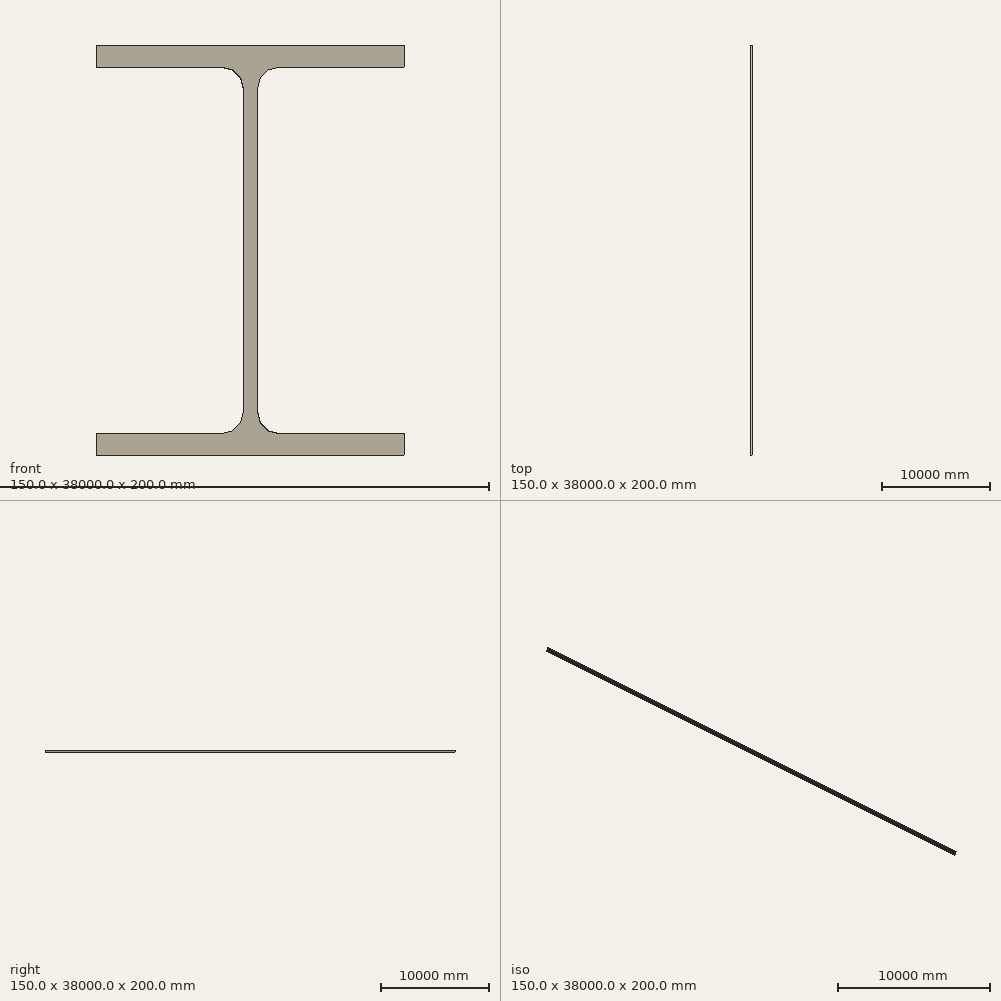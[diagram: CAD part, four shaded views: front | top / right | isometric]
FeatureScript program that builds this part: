
annotation { "Feature Type Name" : "Feature", "Feature Type Description" : "" }
export const myFeature = defineFeature(function(context is Context, id is Id, definition is map)
    precondition{}
    {
        {
            var Q0;
            Q0=qCreatedBy(makeId("Front.planeOp"),FACE);
            var sketch = newSketch(context, id + "F0", { "sketchPlane" : qUnion([Q0])});
            skLineSegment(sketch, "E0.left", {"start": v(3.55, 79.3) * mm, "end": v(3.55, -79.3) * mm});
            skLineSegment(sketch, "E0.right", {"start": v(-3.55, 79.3) * mm, "end": v(-3.55, -79.3) * mm});
            skPoint(sketch, "E0.middle", {"position": v(0, 0) * mm});
            skLineSegment(sketch, "E1.bottom", {"start": v(-75, 89.3) * mm, "end": v(-13.55, 89.3) * mm});
            skLineSegment(sketch, "E1.top", {"start": v(-75, 100) * mm, "end": v(75, 100) * mm});
            skLineSegment(sketch, "E1.left", {"start": v(-75, 89.3) * mm, "end": v(-75, 100) * mm});
            skLineSegment(sketch, "E1.right", {"start": v(75, 89.3) * mm, "end": v(75, 100) * mm});
            skLineSegment(sketch, "E2.bottom", {"start": v(75, -89.3) * mm, "end": v(13.55, -89.3) * mm});
            skLineSegment(sketch, "E2.top", {"start": v(75, -100) * mm, "end": v(-75, -100) * mm});
            skLineSegment(sketch, "E2.left", {"start": v(75, -89.3) * mm, "end": v(75, -100) * mm});
            skLineSegment(sketch, "E2.right", {"start": v(-75, -89.3) * mm, "end": v(-75, -100) * mm});
            skLineSegment(sketch, "E3.trimOffspring", {"start": v(13.55, 89.3) * mm, "end": v(75, 89.3) * mm});
            skLineSegment(sketch, "E4.trimOffspring", {"start": v(-13.55, -89.3) * mm, "end": v(-75, -89.3) * mm});
            skPoint(sketch, "E5.visualSharp", {"position": v(3.55, 89.3) * mm});
            skArc(sketch, "E5.filletArc", {"start": v(13.55, 89.3) * mm, "mid": v(6.48, 86.37) * mm, "end": v(3.55, 79.3) * mm});
            skPoint(sketch, "E6.visualSharp", {"position": v(-3.55, 89.3) * mm});
            skArc(sketch, "E6.filletArc", {"start": v(-3.55, 79.3) * mm, "mid": v(-6.48, 86.37) * mm, "end": v(-13.55, 89.3) * mm});
            skPoint(sketch, "E7.visualSharp", {"position": v(3.55, -89.3) * mm});
            skArc(sketch, "E7.filletArc", {"start": v(3.55, -79.3) * mm, "mid": v(6.48, -86.37) * mm, "end": v(13.55, -89.3) * mm});
            skPoint(sketch, "E8.visualSharp", {"position": v(-3.55, -89.3) * mm});
            skArc(sketch, "E8.filletArc", {"start": v(-13.55, -89.3) * mm, "mid": v(-6.48, -86.37) * mm, "end": v(-3.55, -79.3) * mm});
            skSolve(sketch);
        }
        {
            var Q0;
            Q0 = qSketchRegion(id + "F0", true);
            extrude(context, id + "F1", {"entities" : qUnion([Q0]), "oppositeDirection" : true, "depth" : 38000 * mm});
        }
    });
